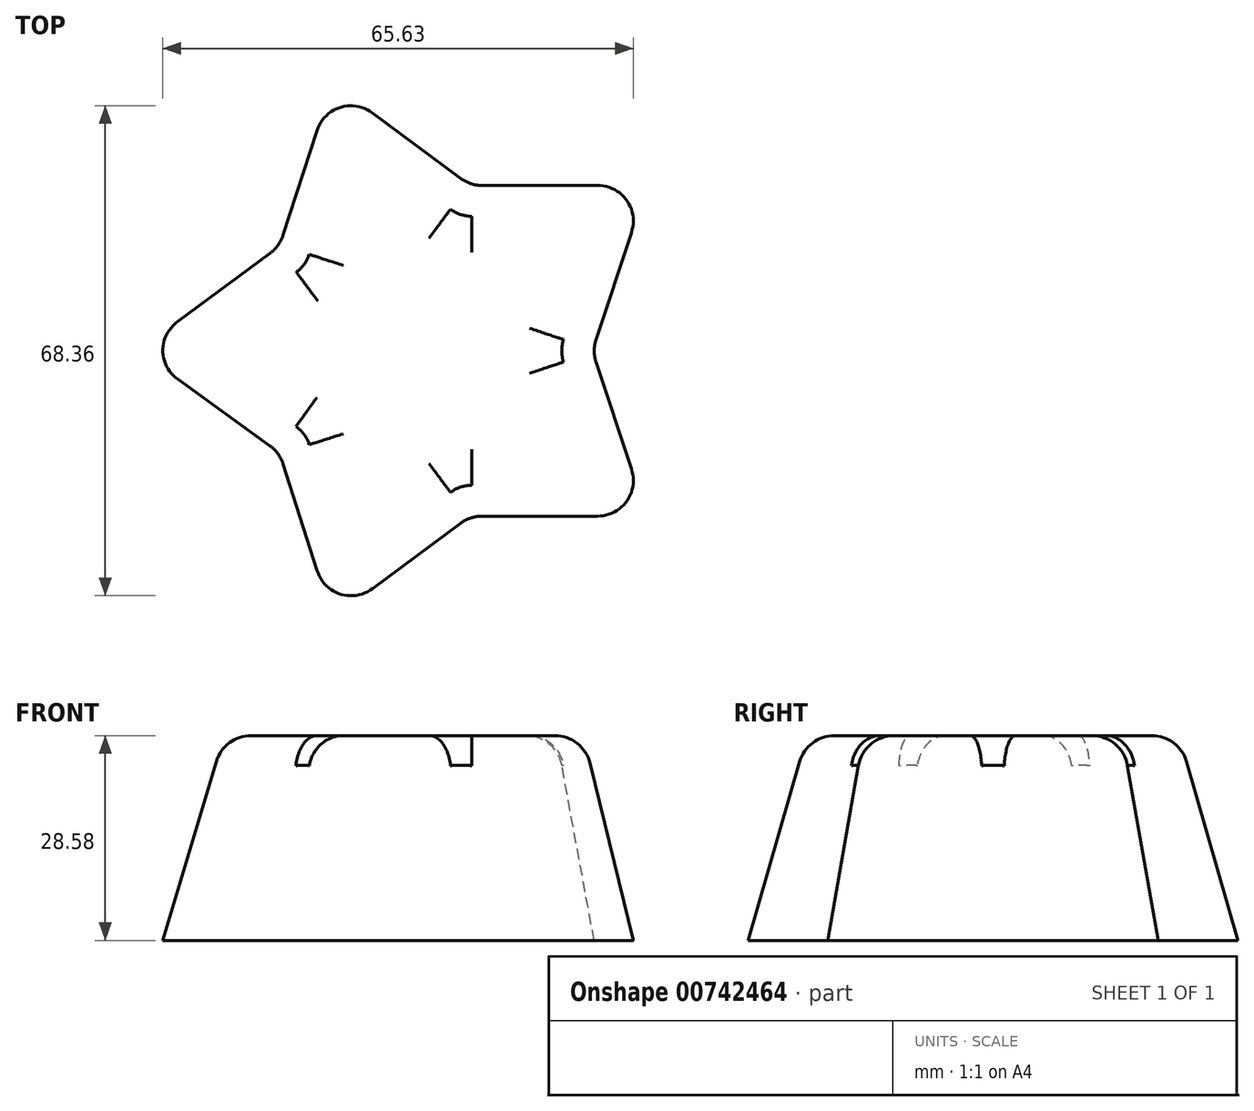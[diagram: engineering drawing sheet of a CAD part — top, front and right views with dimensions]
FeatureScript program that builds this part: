
annotation { "Feature Type Name" : "Feature", "Feature Type Description" : "" }
export const myFeature = defineFeature(function(context is Context, id is Id, definition is map)
    precondition{}
    {
        {
            var Q0;
            Q0=qCreatedBy(makeId("Top.planeOp"),FACE);
            var sketch = newSketch(context, id + "F0", { "sketchPlane" : qUnion([Q0])});
            skCircle(sketch, "E0.cCircle", {"center": v(0, 0) * mm, "radius": 31.75 * mm, "construction": true});
            skLineSegment(sketch, "E0.0", {"start": v(31.75, 23.07) * mm, "end": v(31.75, -23.07) * mm});
            skLineSegment(sketch, "E0.1", {"start": v(31.75, -23.07) * mm, "end": v(-12.13, -37.32) * mm});
            skLineSegment(sketch, "E0.2", {"start": v(-12.13, -37.32) * mm, "end": v(-39.25, 0) * mm});
            skLineSegment(sketch, "E0.3", {"start": v(-39.25, 0) * mm, "end": v(-12.13, 37.32) * mm});
            skLineSegment(sketch, "E0.4", {"start": v(-12.13, 37.32) * mm, "end": v(31.75, 23.07) * mm});
            skPoint(sketch, "E0.0.midPoint", {"position": v(31.75, 0) * mm});
            skLineSegment(sketch, "E1.0", {"start": v(24.13, 17.53) * mm, "end": v(24.13, -17.53) * mm});
            skLineSegment(sketch, "E1.1", {"start": v(-9.22, 28.37) * mm, "end": v(24.13, 17.53) * mm});
            skLineSegment(sketch, "E1.2", {"start": v(24.13, -17.53) * mm, "end": v(-9.22, -28.37) * mm});
            skLineSegment(sketch, "E1.3", {"start": v(-9.22, -28.37) * mm, "end": v(-29.83, 0) * mm});
            skLineSegment(sketch, "E1.4", {"start": v(-29.83, 0) * mm, "end": v(-9.22, 28.37) * mm});
            skLineSegment(sketch, "E2", {"start": v(31.75, 23.07) * mm, "end": v(24.13, 0) * mm});
            skLineSegment(sketch, "E3", {"start": v(24.13, 0) * mm, "end": v(31.75, -23.07) * mm});
            skLineSegment(sketch, "E4", {"start": v(7.1, -23.07) * mm, "end": v(-12.13, -37.32) * mm});
            skLineSegment(sketch, "E5", {"start": v(-19.52, -14.18) * mm, "end": v(-39.25, 0) * mm});
            skLineSegment(sketch, "E6", {"start": v(-19.52, -14.18) * mm, "end": v(-12.13, -37.32) * mm});
            skLineSegment(sketch, "E7", {"start": v(7.1, -23.07) * mm, "end": v(31.75, -23.07) * mm});
            skLineSegment(sketch, "E8", {"start": v(31.75, 23.07) * mm, "end": v(7.1, 23.07) * mm});
            skLineSegment(sketch, "E9", {"start": v(7.1, 23.07) * mm, "end": v(-12.13, 37.32) * mm});
            skLineSegment(sketch, "E10", {"start": v(-12.13, 37.32) * mm, "end": v(-19.52, 14.57) * mm});
            skPoint(sketch, "E10.endSnap0", {"position": v(-19.52, 14.18) * mm});
            skLineSegment(sketch, "E11", {"start": v(-19.52, 14.57) * mm, "end": v(-39.25, 0) * mm});
            skSolve(sketch);
        }
        {
            var Q0;
            {var subQ0=sQuery(id+"F0.wireOp",EDGE,"E1.4");Q0=makeQuery(id+"F0.imprint","IMPRINT",FACE,{"disambiguationData":[TD([[makeQuery(id+"F0.imprint","IMPRINT",EDGE,{"derivedFrom":subQ0}),1.0]])]});}
            var Q1;
            {var subQ4=sQuery(id+"F0.wireOp",EDGE,"E1.4");Q1=makeQuery(id+"F0.imprint","IMPRINT",FACE,{"disambiguationData":[TD([[makeQuery(id+"F0.imprint","IMPRINT",EDGE,{"derivedFrom":subQ4}),-1.0]])]});}
            var Q2;
            {var subQ3=sQuery(id+"F0.wireOp",EDGE,"E2");Q2=makeQuery(id+"F0.imprint","IMPRINT",FACE,{"disambiguationData":[TD([[makeQuery(id+"F0.imprint","IMPRINT",EDGE,{"derivedFrom":subQ3}),-1.0]])]});}
            var Q3;
            {var subQ3=sQuery(id+"F0.wireOp",EDGE,"E3");Q3=makeQuery(id+"F0.imprint","IMPRINT",FACE,{"disambiguationData":[TD([[makeQuery(id+"F0.imprint","IMPRINT",EDGE,{"derivedFrom":subQ3}),-1.0]])]});}
            var Q4;
            {var subQ3=sQuery(id+"F0.wireOp",EDGE,"E4");Q4=makeQuery(id+"F0.imprint","IMPRINT",FACE,{"disambiguationData":[TD([[makeQuery(id+"F0.imprint","IMPRINT",EDGE,{"derivedFrom":subQ3}),-1.0]])]});}
            extrude(context, id + "F1", {"entities" : qUnion([Q0, Q1, Q2, Q3, Q4]), "depth" : 28.57 * mm, "offsetDistance" : 25.4 * mm, "hasDraft" : true, "draftAngle" : 10 * degree, "draftPullDirection" : true});
        }
        {
            var Q0;
            Q0=makeQuery(id+"F1.opExtrude","CAP_FACE",FACE,{"disambiguationData":[OSD([sQuery(id+"F0.wireOp",EDGE,"E2"),sQuery(id+"F0.wireOp",EDGE,"E3"),sQuery(id+"F0.wireOp",EDGE,"E4"),sQuery(id+"F0.wireOp",EDGE,"E5"),sQuery(id+"F0.wireOp",EDGE,"E6"),sQuery(id+"F0.wireOp",EDGE,"E7"),sQuery(id+"F0.wireOp",EDGE,"E8"),sQuery(id+"F0.wireOp",EDGE,"E9"),sQuery(id+"F0.wireOp",EDGE,"E10"),sQuery(id+"F0.wireOp",EDGE,"E11")])],"isStart":false});
            var Q1;
            Q1=makeQuery(id+"F1.opExtrude","SWEPT_EDGE",EDGE,{"disambiguationData":[OSD([sQuery(id+"F0.wireOp",EDGE,"E0.0"),sQuery(id+"F0.wireOp",EDGE,"E0.1"),sQuery(id+"F0.wireOp",EDGE,"E3"),sQuery(id+"F0.wireOp",EDGE,"E7")])]});
            var Q2;
            Q2=makeQuery(id+"F1.opExtrude","SWEPT_EDGE",EDGE,{"disambiguationData":[OSD([sQuery(id+"F0.wireOp",EDGE,"E1.2"),sQuery(id+"F0.wireOp",EDGE,"E4"),sQuery(id+"F0.wireOp",EDGE,"E7")])]});
            var Q3;
            Q3=makeQuery(id+"F1.opExtrude","SWEPT_EDGE",EDGE,{"disambiguationData":[OSD([sQuery(id+"F0.wireOp",EDGE,"E0.1"),sQuery(id+"F0.wireOp",EDGE,"E0.2"),sQuery(id+"F0.wireOp",EDGE,"E4"),sQuery(id+"F0.wireOp",EDGE,"E6")])]});
            var Q4;
            Q4=makeQuery(id+"F1.opExtrude","SWEPT_EDGE",EDGE,{"disambiguationData":[OSD([sQuery(id+"F0.wireOp",EDGE,"E1.3"),sQuery(id+"F0.wireOp",EDGE,"E5"),sQuery(id+"F0.wireOp",EDGE,"E6")])]});
            var Q5;
            Q5=makeQuery(id+"F1.opExtrude","SWEPT_EDGE",EDGE,{"disambiguationData":[OSD([sQuery(id+"F0.wireOp",EDGE,"E0.2"),sQuery(id+"F0.wireOp",EDGE,"E0.3"),sQuery(id+"F0.wireOp",EDGE,"E5"),sQuery(id+"F0.wireOp",EDGE,"E11")])]});
            var Q6;
            Q6=makeQuery(id+"F1.opExtrude","SWEPT_EDGE",EDGE,{"disambiguationData":[OSD([sQuery(id+"F0.wireOp",EDGE,"E10"),sQuery(id+"F0.wireOp",EDGE,"E11")])]});
            var Q7;
            Q7=makeQuery(id+"F1.opExtrude","SWEPT_EDGE",EDGE,{"disambiguationData":[OSD([sQuery(id+"F0.wireOp",EDGE,"E0.3"),sQuery(id+"F0.wireOp",EDGE,"E0.4"),sQuery(id+"F0.wireOp",EDGE,"E9"),sQuery(id+"F0.wireOp",EDGE,"E10")])]});
            var Q8;
            Q8=makeQuery(id+"F1.opExtrude","SWEPT_EDGE",EDGE,{"disambiguationData":[OSD([sQuery(id+"F0.wireOp",EDGE,"E1.1"),sQuery(id+"F0.wireOp",EDGE,"E8"),sQuery(id+"F0.wireOp",EDGE,"E9")])]});
            var Q9;
            Q9=makeQuery(id+"F1.opExtrude","SWEPT_EDGE",EDGE,{"disambiguationData":[OSD([sQuery(id+"F0.wireOp",EDGE,"E1.0"),sQuery(id+"F0.wireOp",EDGE,"E2"),sQuery(id+"F0.wireOp",EDGE,"E3")])]});
            var Q10;
            Q10=makeQuery(id+"F1.opExtrude","SWEPT_EDGE",EDGE,{"disambiguationData":[OSD([sQuery(id+"F0.wireOp",EDGE,"E0.0"),sQuery(id+"F0.wireOp",EDGE,"E0.4"),sQuery(id+"F0.wireOp",EDGE,"E2"),sQuery(id+"F0.wireOp",EDGE,"E8")])]});
            fillet(context, id + "F2", {"entities" : qUnion([Q0, Q1, Q2, Q3, Q4, Q5, Q6, Q7, Q8, Q9, Q10]), "radius" : 5.08 * mm, "tangentPropagation" : true, "allowEdgeOverflow" : false});
        }
    });
